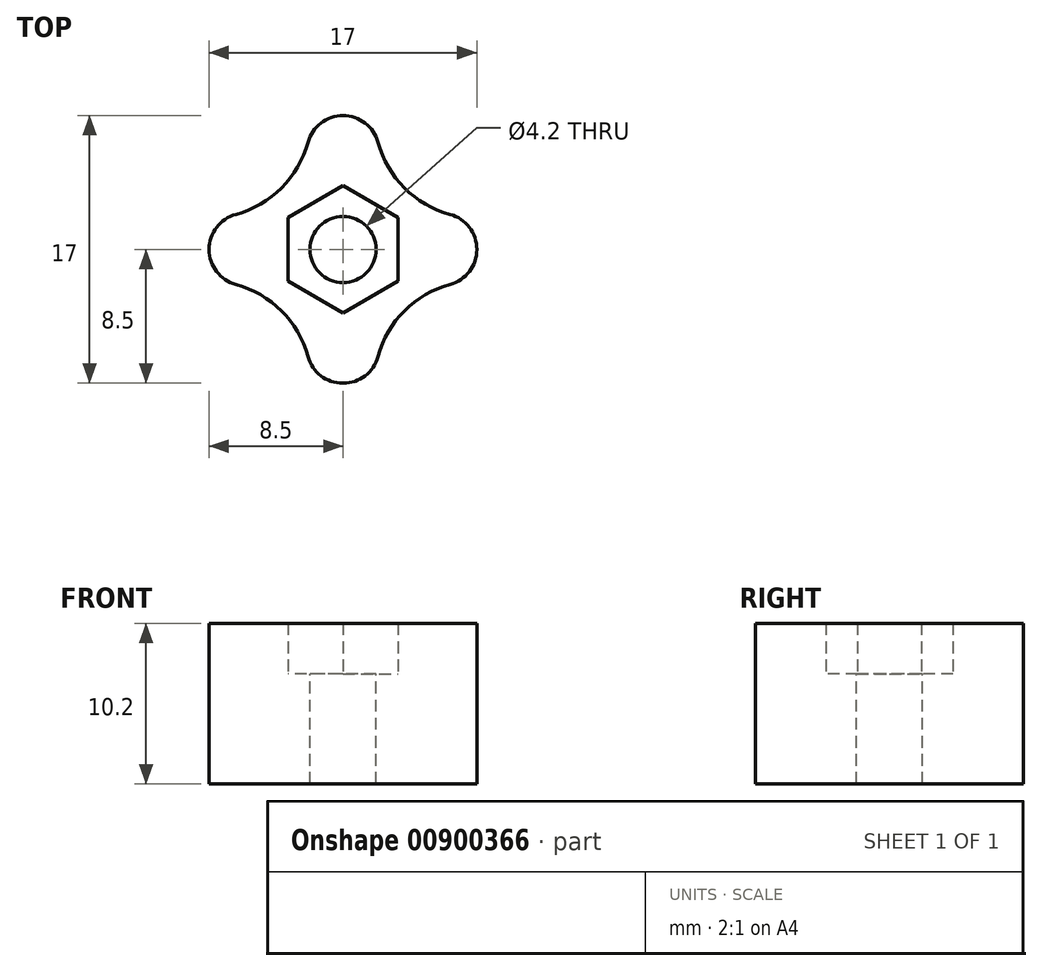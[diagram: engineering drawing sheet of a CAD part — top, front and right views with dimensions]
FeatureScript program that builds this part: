
annotation { "Feature Type Name" : "Feature", "Feature Type Description" : "" }
export const myFeature = defineFeature(function(context is Context, id is Id, definition is map)
    precondition{}
    {
        {
            var Q0;
            Q0=qCreatedBy(makeId("Top.planeOp"),FACE);
            var sketch = newSketch(context, id + "F0", { "sketchPlane" : qUnion([Q0])});
            skCircle(sketch, "E0", {"center": v(0, 0) * mm, "radius": 2.1 * mm});
            skCircle(sketch, "E1.cCircle", {"center": v(0, 0) * mm, "radius": 3.5 * mm, "construction": true});
            skLineSegment(sketch, "E1.0", {"start": v(3.5, 2.02) * mm, "end": v(3.5, -2.02) * mm});
            skLineSegment(sketch, "E1.1", {"start": v(3.5, -2.02) * mm, "end": v(0, -4.04) * mm});
            skLineSegment(sketch, "E1.2", {"start": v(0, -4.04) * mm, "end": v(-3.5, -2.02) * mm});
            skLineSegment(sketch, "E1.3", {"start": v(-3.5, -2.02) * mm, "end": v(-3.5, 2.02) * mm});
            skLineSegment(sketch, "E1.4", {"start": v(-3.5, 2.02) * mm, "end": v(0, 4.04) * mm});
            skLineSegment(sketch, "E1.5", {"start": v(0, 4.04) * mm, "end": v(3.5, 2.02) * mm});
            skPoint(sketch, "E1.0.midPoint", {"position": v(3.5, 0) * mm});
            skLineSegment(sketch, "E2", {"start": v(0, 4.04) * mm, "end": v(0, -4.04) * mm, "construction": true});
            skLineSegment(sketch, "E3", {"start": v(3.5, 0) * mm, "end": v(-3.5, 0) * mm, "construction": true});
            skLineSegment(sketch, "E4", {"start": v(8.5, 8.5) * mm, "end": v(8.5, 0) * mm});
            skLineSegment(sketch, "E5", {"start": v(0, 8.5) * mm, "end": v(8.5, 8.5) * mm});
            skArc(sketch, "E6", {"start": v(2, 8.5) * mm, "mid": v(3.9, 3.9) * mm, "end": v(8.5, 2) * mm});
            skLineSegment(sketch, "E7.MirrorCS", {"start": v(0, -8.5) * mm, "end": v(8.5, -8.5) * mm});
            skArc(sketch, "E8.MirrorCS", {"start": v(2, -8.5) * mm, "mid": v(3.9, -3.9) * mm, "end": v(8.5, -2) * mm});
            skLineSegment(sketch, "E9.MirrorCS", {"start": v(8.5, -8.5) * mm, "end": v(8.5, 0) * mm});
            skLineSegment(sketch, "E10.MirrorCS", {"start": v(0, 8.5) * mm, "end": v(-8.5, 8.5) * mm});
            skArc(sketch, "E11.MirrorCS", {"start": v(-2, 8.5) * mm, "mid": v(-3.9, 3.9) * mm, "end": v(-8.5, 2) * mm});
            skArc(sketch, "E12.MirrorCS", {"start": v(-2, -8.5) * mm, "mid": v(-3.9, -3.9) * mm, "end": v(-8.5, -2) * mm});
            skLineSegment(sketch, "E13.MirrorCS", {"start": v(0, -8.5) * mm, "end": v(-8.5, -8.5) * mm});
            skLineSegment(sketch, "E14.MirrorCS", {"start": v(-8.5, -8.5) * mm, "end": v(-8.5, 0) * mm});
            skLineSegment(sketch, "E15.MirrorCS", {"start": v(-8.5, 8.5) * mm, "end": v(-8.5, 0) * mm});
            skSolve(sketch);
        }
        {
            var Q0;
            Q0=makeQuery(id+"F0.imprint","IMPRINT",FACE,{"disambiguationData":[TD([[makeQuery(id+"F0.imprint","IMPRINT",EDGE,{"derivedFrom":sQuery(id+"F0.wireOp",EDGE,"E1.0")}),1.0]])]});
            extrude(context, id + "F1", {"entities" : qUnion([Q0]), "depth" : 3.2 * mm, "offsetDistance" : 25 * mm});
        }
        {
            var Q0;
            Q0=makeQuery(id+"F0.imprint","IMPRINT",FACE,{"disambiguationData":[TD([[makeQuery(id+"F0.imprint","IMPRINT",EDGE,{"derivedFrom":sQuery(id+"F0.wireOp",EDGE,"E0")}),-1.0]])]});
            var Q1;
            Q1=makeQuery(id+"F0.imprint","IMPRINT",FACE,{"disambiguationData":[TD([[makeQuery(id+"F0.imprint","IMPRINT",EDGE,{"derivedFrom":sQuery(id+"F0.wireOp",EDGE,"E1.0")}),1.0]])]});
            extrude(context, id + "F2", {"entities" : qUnion([Q0, Q1]), "operationType" : NewBodyOperationType.ADD, "oppositeDirection" : true, "depth" : 7 * mm, "offsetDistance" : 25 * mm});
        }
        {
            var Q0;
            {var subQ0=sQuery(id+"F0.wireOp",EDGE,"E6");var subQ1=sQuery(id+"F0.wireOp",EDGE,"E4");Q0=makeQuery(id+"F2.boolean.opBoolean","MERGE",EDGE,{"derivedFrom":[makeQuery(id+"F1.opExtrude","SWEPT_EDGE",EDGE,{"disambiguationData":[OSD([subQ1,subQ0])]}),makeQuery(id+"F2.opExtrude","SWEPT_EDGE",EDGE,{"disambiguationData":[OSD([subQ1,subQ0])]})]});}
            var Q1;
            {var subQ0=sQuery(id+"F0.wireOp",EDGE,"E9.MirrorCS");var subQ1=sQuery(id+"F0.wireOp",EDGE,"E8.MirrorCS");Q1=makeQuery(id+"F2.boolean.opBoolean","MERGE",EDGE,{"derivedFrom":[makeQuery(id+"F1.opExtrude","SWEPT_EDGE",EDGE,{"disambiguationData":[OSD([subQ1,subQ0])]}),makeQuery(id+"F2.opExtrude","SWEPT_EDGE",EDGE,{"disambiguationData":[OSD([subQ1,subQ0])]})]});}
            var Q2;
            {var subQ0=sQuery(id+"F0.wireOp",EDGE,"E8.MirrorCS");var subQ1=sQuery(id+"F0.wireOp",EDGE,"E7.MirrorCS");Q2=makeQuery(id+"F2.boolean.opBoolean","MERGE",EDGE,{"derivedFrom":[makeQuery(id+"F1.opExtrude","SWEPT_EDGE",EDGE,{"disambiguationData":[OSD([subQ1,subQ0])]}),makeQuery(id+"F2.opExtrude","SWEPT_EDGE",EDGE,{"disambiguationData":[OSD([subQ1,subQ0])]})]});}
            var Q3;
            {var subQ0=sQuery(id+"F0.wireOp",EDGE,"E6");var subQ1=sQuery(id+"F0.wireOp",EDGE,"E5");Q3=makeQuery(id+"F2.boolean.opBoolean","MERGE",EDGE,{"derivedFrom":[makeQuery(id+"F1.opExtrude","SWEPT_EDGE",EDGE,{"disambiguationData":[OSD([subQ1,subQ0])]}),makeQuery(id+"F2.opExtrude","SWEPT_EDGE",EDGE,{"disambiguationData":[OSD([subQ1,subQ0])]})]});}
            var Q4;
            {var subQ0=sQuery(id+"F0.wireOp",EDGE,"E11.MirrorCS");var subQ1=sQuery(id+"F0.wireOp",EDGE,"E10.MirrorCS");Q4=makeQuery(id+"F2.boolean.opBoolean","MERGE",EDGE,{"derivedFrom":[makeQuery(id+"F1.opExtrude","SWEPT_EDGE",EDGE,{"disambiguationData":[OSD([subQ1,subQ0])]}),makeQuery(id+"F2.opExtrude","SWEPT_EDGE",EDGE,{"disambiguationData":[OSD([subQ1,subQ0])]})]});}
            var Q5;
            {var subQ0=sQuery(id+"F0.wireOp",EDGE,"E15.MirrorCS");var subQ1=sQuery(id+"F0.wireOp",EDGE,"E11.MirrorCS");Q5=makeQuery(id+"F2.boolean.opBoolean","MERGE",EDGE,{"derivedFrom":[makeQuery(id+"F1.opExtrude","SWEPT_EDGE",EDGE,{"disambiguationData":[OSD([subQ1,subQ0])]}),makeQuery(id+"F2.opExtrude","SWEPT_EDGE",EDGE,{"disambiguationData":[OSD([subQ1,subQ0])]})]});}
            var Q6;
            {var subQ0=sQuery(id+"F0.wireOp",EDGE,"E14.MirrorCS");var subQ1=sQuery(id+"F0.wireOp",EDGE,"E12.MirrorCS");Q6=makeQuery(id+"F2.boolean.opBoolean","MERGE",EDGE,{"derivedFrom":[makeQuery(id+"F1.opExtrude","SWEPT_EDGE",EDGE,{"disambiguationData":[OSD([subQ1,subQ0])]}),makeQuery(id+"F2.opExtrude","SWEPT_EDGE",EDGE,{"disambiguationData":[OSD([subQ1,subQ0])]})]});}
            var Q7;
            {var subQ0=sQuery(id+"F0.wireOp",EDGE,"E13.MirrorCS");var subQ1=sQuery(id+"F0.wireOp",EDGE,"E12.MirrorCS");Q7=makeQuery(id+"F2.boolean.opBoolean","MERGE",EDGE,{"derivedFrom":[makeQuery(id+"F1.opExtrude","SWEPT_EDGE",EDGE,{"disambiguationData":[OSD([subQ1,subQ0])]}),makeQuery(id+"F2.opExtrude","SWEPT_EDGE",EDGE,{"disambiguationData":[OSD([subQ1,subQ0])]})]});}
            fillet(context, id + "F3", {"entities" : qUnion([Q0, Q1, Q2, Q3, Q4, Q5, Q6, Q7]), "radius" : 2.3 * mm, "tangentPropagation" : true, "allowEdgeOverflow" : false});
        }
    });
